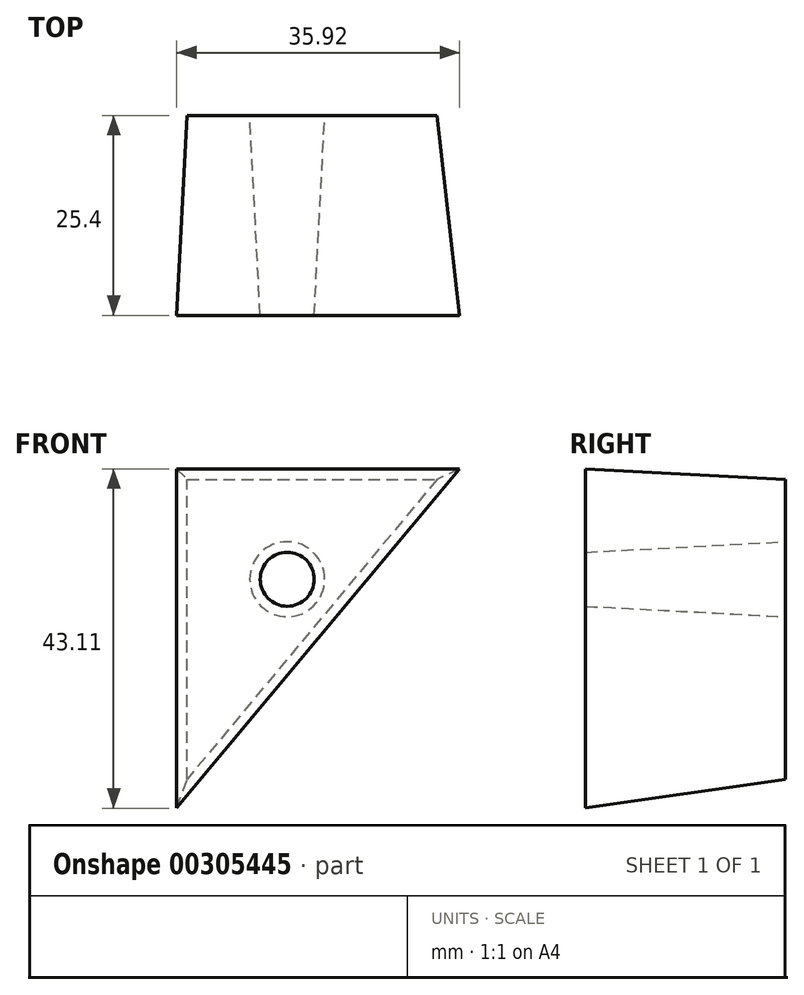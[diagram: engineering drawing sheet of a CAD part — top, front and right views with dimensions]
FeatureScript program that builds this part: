
annotation { "Feature Type Name" : "Feature", "Feature Type Description" : "" }
export const myFeature = defineFeature(function(context is Context, id is Id, definition is map)
    precondition{}
    {
        {
            var Q0;
            Q0=qCreatedBy(makeId("Front.planeOp"),FACE);
            var sketch = newSketch(context, id + "F0", { "sketchPlane" : qUnion([Q0])});
            skLineSegment(sketch, "E0", {"start": v(0, 0) * mm, "end": v(0, 38.1) * mm});
            skLineSegment(sketch, "E1", {"start": v(0, 38.1) * mm, "end": v(31.75, 38.1) * mm});
            skLineSegment(sketch, "E2", {"start": v(31.75, 38.1) * mm, "end": v(0, 0) * mm});
            skCircle(sketch, "E3", {"center": v(12.7, 25.4) * mm, "radius": 4.76 * mm});
            skSolve(sketch);
        }
        {
            var Q0;
            Q0=makeQuery(id+"F0.imprint","IMPRINT",FACE,{"disambiguationData":[TD([[makeQuery(id+"F0.imprint","IMPRINT",EDGE,{"derivedFrom":sQuery(id+"F0.wireOp",EDGE,"E0")}),-1.0]])]});
            extrude(context, id + "F1", {"entities" : qUnion([Q0]), "depth" : 25.4 * mm, "hasDraft" : true, "draftAngle" : 3 * degree});
        }
    });
